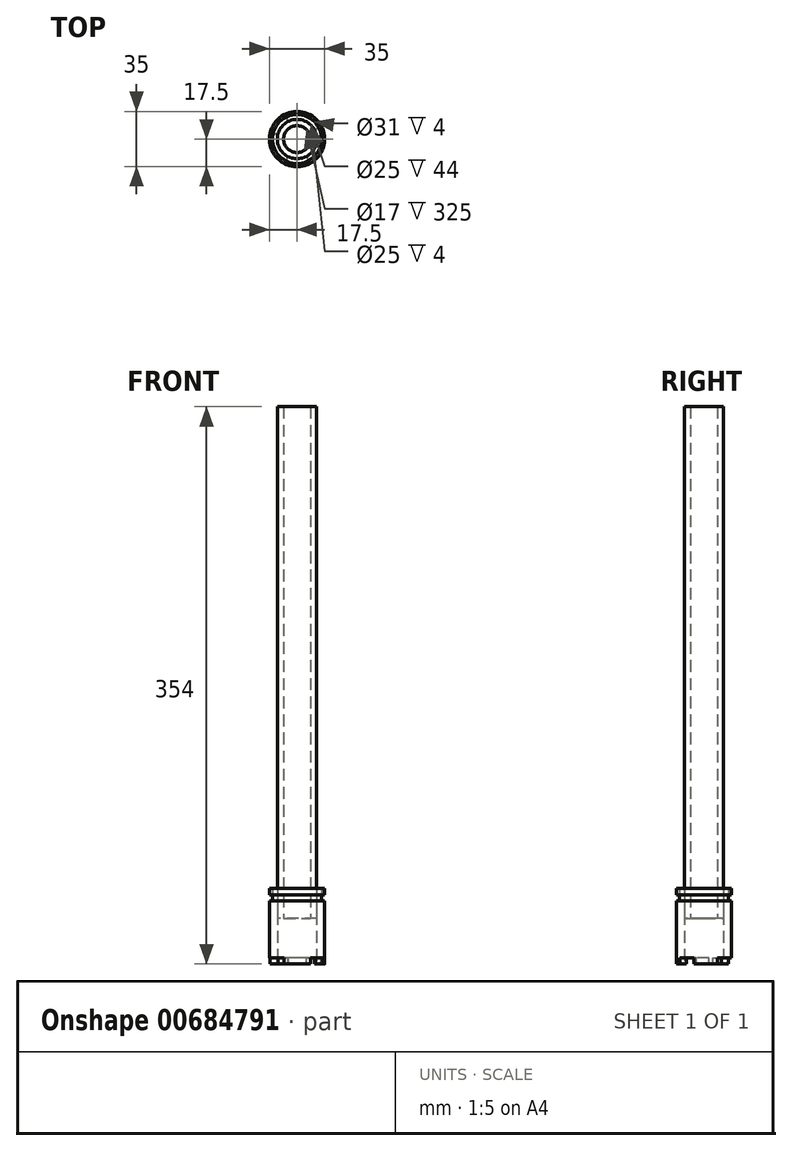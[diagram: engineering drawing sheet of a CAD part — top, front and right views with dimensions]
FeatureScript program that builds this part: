
annotation { "Feature Type Name" : "Feature", "Feature Type Description" : "" }
export const myFeature = defineFeature(function(context is Context, id is Id, definition is map)
    precondition{}
    {
        {
            var Q0;
            Q0=qCreatedBy(makeId("Top.planeOp"),FACE);
            var sketch = newSketch(context, id + "F0", { "sketchPlane" : qUnion([Q0])});
            skCircle(sketch, "E0", {"center": v(0, 0) * mm, "radius": 17.5 * mm});
            skCircle(sketch, "E1", {"center": v(0, 0) * mm, "radius": 12.5 * mm});
            skSolve(sketch);
        }
        {
            var Q0;
            Q0=makeQuery(id+"F0.imprint","IMPRINT",FACE,{"disambiguationData":[TD([[makeQuery(id+"F0.imprint","IMPRINT",EDGE,{"derivedFrom":sQuery(id+"F0.wireOp",EDGE,"E0")}),1.0]])]});
            extrude(context, id + "F1", {"entities" : qUnion([Q0]), "depth" : 36 * mm, "offsetDistance" : 25 * mm});
        }
        {
            var Q0;
            Q0=makeQuery(id+"F1.opExtrude","CAP_FACE",FACE,{"disambiguationData":[OSD([sQuery(id+"F0.wireOp",EDGE,"E0"),sQuery(id+"F0.wireOp",EDGE,"E1")])],"isStart":false});
            var sketch = newSketch(context, id + "F2", { "sketchPlane" : qUnion([Q0])});
            skCircle(sketch, "E2", {"center": v(0, 0) * mm, "radius": 12.5 * mm});
            skCircle(sketch, "E3", {"center": v(0, 0) * mm, "radius": 15.5 * mm});
            skSolve(sketch);
        }
        {
            var Q0;
            Q0=makeQuery(id+"F2.imprint","IMPRINT",FACE,{"disambiguationData":[TD([[makeQuery(id+"F2.imprint","IMPRINT",EDGE,{"derivedFrom":sQuery(id+"F2.wireOp",EDGE,"E2")}),-1.0]])]});
            extrude(context, id + "F3", {"entities" : qUnion([Q0]), "operationType" : NewBodyOperationType.ADD, "depth" : 4 * mm, "offsetDistance" : 25 * mm});
        }
        {
            var Q0;
            Q0=makeQuery(id+"F3.opExtrude","CAP_FACE",FACE,{"disambiguationData":[OSD([sQuery(id+"F2.wireOp",EDGE,"E2"),sQuery(id+"F2.wireOp",EDGE,"E3")])],"isStart":false});
            var sketch = newSketch(context, id + "F4", { "sketchPlane" : qUnion([Q0])});
            skCircle(sketch, "E4", {"center": v(0, 0) * mm, "radius": 12.5 * mm});
            skPoint(sketch, "E4.first.point", {"position": v(1.58, 12.4) * mm});
            skPoint(sketch, "E4.second.point", {"position": v(1.2, -12.44) * mm});
            skPoint(sketch, "E4.third.point", {"position": v(12.5, 0) * mm});
            skCircle(sketch, "E5", {"center": v(0, 0) * mm, "radius": 17.5 * mm});
            skSolve(sketch);
        }
        {
            var Q0;
            Q0=makeQuery(id+"F4.imprint","IMPRINT",FACE,{"disambiguationData":[TD([[makeQuery(id+"F4.imprint","IMPRINT",EDGE,{"derivedFrom":sQuery(id+"F4.wireOp",EDGE,"E4")}),1.0]])]});
            var Q1;
            Q1=makeQuery(id+"F4.imprint","IMPRINT",FACE,{"disambiguationData":[TD([[makeQuery(id+"F4.imprint","IMPRINT",EDGE,{"derivedFrom":sQuery(id+"F4.wireOp",EDGE,"E5")}),1.0]])]});
            extrude(context, id + "F5", {"entities" : qUnion([Q0, Q1]), "depth" : 4 * mm, "offsetDistance" : 25 * mm});
        }
        {
            var Q0;
            Q0=makeQuery(id+"F3.opExtrude","CAP_FACE",FACE,{"disambiguationData":[OSD([sQuery(id+"F2.wireOp",EDGE,"E2"),sQuery(id+"F2.wireOp",EDGE,"E3")])],"isStart":false});
            extrude(context, id + "F6", {"entities" : qUnion([Q0]), "depth" : 4 * mm, "offsetDistance" : 25 * mm});
        }
        {
            var Q0;
            Q0=makeQuery(id+"F5.opExtrude","CAP_FACE",FACE,{"disambiguationData":[OSD([sQuery(id+"F4.wireOp",EDGE,"E4")])],"isStart":false});
            extrude(context, id + "F7", {"entities" : qUnion([Q0]), "operationType" : NewBodyOperationType.REMOVE, "oppositeDirection" : true, "depth" : 25 * mm, "offsetDistance" : 25 * mm});
        }
        {
            var Q0;
            Q0=qCreatedBy(makeId("Right.planeOp"),FACE);
            var sketch = newSketch(context, id + "F8", { "sketchPlane" : qUnion([Q0])});
            skLineSegment(sketch, "E6", {"start": v(17.36, 43.88) * mm, "end": v(13.77, 47.47) * mm});
            skLineSegment(sketch, "E7", {"start": v(13.77, 47.47) * mm, "end": v(12.26, 48.98) * mm});
            skLineSegment(sketch, "E8", {"start": v(12.26, 43.88) * mm, "end": v(17.36, 43.88) * mm});
            skLineSegment(sketch, "E9", {"start": v(12.26, 43.88) * mm, "end": v(12.26, 48.98) * mm});
            skSolve(sketch);
        }
        {
            var Q0;
            Q0=sQuery(id+"F8.wireOp",EDGE,"E8");
            var Q1;
            Q1=sQuery(id+"F8.wireOp",EDGE,"E6");
            var Q2;
            Q2=sQuery(id+"F8.wireOp",EDGE,"E7");
            var Q3;
            Q3=sQuery(id+"F8.wireOp",EDGE,"E9");
            var Q4;
            Q4=makeQuery(id+"F3.boolean.opBoolean","MERGE",FACE,{"derivedFrom":[makeQuery(id+"F1.opExtrude","SWEPT_FACE",FACE,{"disambiguationData":[OSD([sQuery(id+"F0.wireOp",EDGE,"E1")])]}),makeQuery(id+"F3.opExtrude","SWEPT_FACE",FACE,{"disambiguationData":[OSD([sQuery(id+"F2.wireOp",EDGE,"E2")])]})]});
            revolve(context, id + "F9", {"bodyType" : ToolBodyType.SURFACE, "surfaceEntities" : qUnion([Q0, Q1, Q2, Q3]), "axis" : qUnion([Q4]), "revolveType" : RevolveType.FULL});
        }
        {
            var Q0;
            Q0=makeQuery(id+"F1.opExtrude","CAP_FACE",FACE,{"disambiguationData":[OSD([sQuery(id+"F0.wireOp",EDGE,"E0"),sQuery(id+"F0.wireOp",EDGE,"E1")])],"isStart":true});
            var sketch = newSketch(context, id + "F10", { "sketchPlane" : qUnion([Q0])});
            skCircle(sketch, "E10", {"center": v(0, 0) * mm, "radius": 12.5 * mm});
            skPoint(sketch, "E10.first.point", {"position": v(10.83, -6.25) * mm});
            skPoint(sketch, "E10.second.point", {"position": v(-12.5, 0) * mm});
            skPoint(sketch, "E10.third.point", {"position": v(5.62, 11.16) * mm});
            skCircle(sketch, "E11", {"center": v(0, 0) * mm, "radius": 8.5 * mm});
            skSolve(sketch);
        }
        {
            var Q0;
            Q0=makeQuery(id+"F10.imprint","IMPRINT",FACE,{"disambiguationData":[TD([[makeQuery(id+"F10.imprint","IMPRINT",EDGE,{"derivedFrom":sQuery(id+"F10.wireOp",EDGE,"E10")}),-1.0]])]});
            extrude(context, id + "F11", {"entities" : qUnion([Q0]), "oppositeDirection" : true, "depth" : 350 * mm, "offsetDistance" : 25 * mm});
        }
        {
            var Q0;
            Q0=makeQuery(id+"F11.opExtrude","CAP_FACE",FACE,{"disambiguationData":[OSD([sQuery(id+"F10.wireOp",EDGE,"E10"),sQuery(id+"F10.wireOp",EDGE,"E11")])],"isStart":true});
            var sketch = newSketch(context, id + "F12", { "sketchPlane" : qUnion([Q0])});
            skCircle(sketch, "E12", {"center": v(0, 0) * mm, "radius": 8.5 * mm});
            skPoint(sketch, "E12.first.point", {"position": v(-7.03, 4.77) * mm});
            skPoint(sketch, "E12.second.point", {"position": v(7.3, -4.36) * mm});
            skPoint(sketch, "E12.third.point", {"position": v(4.5, 7.21) * mm});
            skCircle(sketch, "E13", {"center": v(0, 0) * mm, "radius": 12.5 * mm});
            skPoint(sketch, "E13.first.point", {"position": v(9.5, -8.14) * mm});
            skPoint(sketch, "E13.second.point", {"position": v(-12.5, 0) * mm});
            skPoint(sketch, "E13.third.point", {"position": v(8.09, 9.53) * mm});
            skSolve(sketch);
        }
        {
            var Q0;
            Q0=makeQuery(id+"F12.imprint","IMPRINT",FACE,{"disambiguationData":[TD([[makeQuery(id+"F12.imprint","IMPRINT",EDGE,{"derivedFrom":sQuery(id+"F12.wireOp",EDGE,"E12")}),-1.0]])]});
            extrude(context, id + "F13", {"entities" : qUnion([Q0]), "operationType" : NewBodyOperationType.REMOVE, "oppositeDirection" : true, "depth" : 25 * mm, "offsetDistance" : 25 * mm});
        }
        {
            var Q0;
            Q0=makeQuery(id+"F1.opExtrude","CAP_FACE",FACE,{"disambiguationData":[OSD([sQuery(id+"F0.wireOp",EDGE,"E0"),sQuery(id+"F0.wireOp",EDGE,"E1")])],"isStart":true});
            var sketch = newSketch(context, id + "F14", { "sketchPlane" : qUnion([Q0])});
            skArc(sketch, "E14", {"start": v(-12.06, -3.3) * mm, "mid": v(-9.59, -8.02) * mm, "end": v(-5.38, -11.28) * mm});
            skPoint(sketch, "E14.first.point", {"position": v(-0.74, 12.48) * mm});
            skPoint(sketch, "E14.second.point", {"position": v(1.67, -12.39) * mm});
            skPoint(sketch, "E14.third.point", {"position": v(-12.4, 1.53) * mm});
            skArc(sketch, "E15", {"start": v(-17.19, -3.3) * mm, "mid": v(-13.95, -10.57) * mm, "end": v(-7.83, -15.65) * mm});
            skPoint(sketch, "E15.first.point", {"position": v(-15.28, 8.54) * mm});
            skPoint(sketch, "E15.second.point", {"position": v(17.23, -3.04) * mm});
            skPoint(sketch, "E15.third.point", {"position": v(-3.12, -17.22) * mm});
            skLineSegment(sketch, "E16", {"start": v(11.64, 4.56) * mm, "end": v(16.32, 6.3) * mm});
            skLineSegment(sketch, "E17", {"start": v(11.14, -5.67) * mm, "end": v(15.18, -8.71) * mm});
            skLineSegment(sketch, "E18", {"start": v(-5.84, 11.05) * mm, "end": v(-8.22, 15.45) * mm});
            skLineSegment(sketch, "E19", {"start": v(5.98, 10.97) * mm, "end": v(8.7, 15.18) * mm});
            skLineSegment(sketch, "E20", {"start": v(-12.06, -3.3) * mm, "end": v(-17.19, -3.3) * mm});
            skLineSegment(sketch, "E21", {"start": v(-5.38, -11.28) * mm, "end": v(-7.83, -15.65) * mm});
            skArc(sketch, "E22.trimOffspring", {"start": v(8.7, 15.18) * mm, "mid": v(0.28, 17.5) * mm, "end": v(-8.22, 15.45) * mm});
            skArc(sketch, "E23.trimOffspring", {"start": v(5.98, 10.97) * mm, "mid": v(0.08, 12.5) * mm, "end": v(-5.84, 11.05) * mm});
            skArc(sketch, "E24.trimOffspring", {"start": v(11.14, -5.67) * mm, "mid": v(12.49, -0.6) * mm, "end": v(11.64, 4.56) * mm});
            skArc(sketch, "E25.trimOffspring", {"start": v(15.18, -8.71) * mm, "mid": v(17.45, -1.33) * mm, "end": v(16.32, 6.3) * mm});
            skSolve(sketch);
        }
        {
            var Q0;
            Q0=makeQuery(id+"F14.imprint","IMPRINT",FACE,{"disambiguationData":[TD([[makeQuery(id+"F14.imprint","IMPRINT",EDGE,{"derivedFrom":sQuery(id+"F14.wireOp",EDGE,"E18")}),-1.0]])]});
            var Q1;
            Q1=makeQuery(id+"F14.imprint","IMPRINT",FACE,{"disambiguationData":[TD([[makeQuery(id+"F14.imprint","IMPRINT",EDGE,{"derivedFrom":sQuery(id+"F14.wireOp",EDGE,"E16")}),-1.0]])]});
            var Q2;
            Q2=makeQuery(id+"F14.imprint","IMPRINT",FACE,{"disambiguationData":[TD([[makeQuery(id+"F14.imprint","IMPRINT",EDGE,{"derivedFrom":sQuery(id+"F14.wireOp",EDGE,"E14")}),1.0]])]});
            extrude(context, id + "F15", {"entities" : qUnion([Q0, Q1, Q2]), "operationType" : NewBodyOperationType.ADD, "depth" : 4 * mm, "offsetDistance" : 25 * mm});
        }
    });
